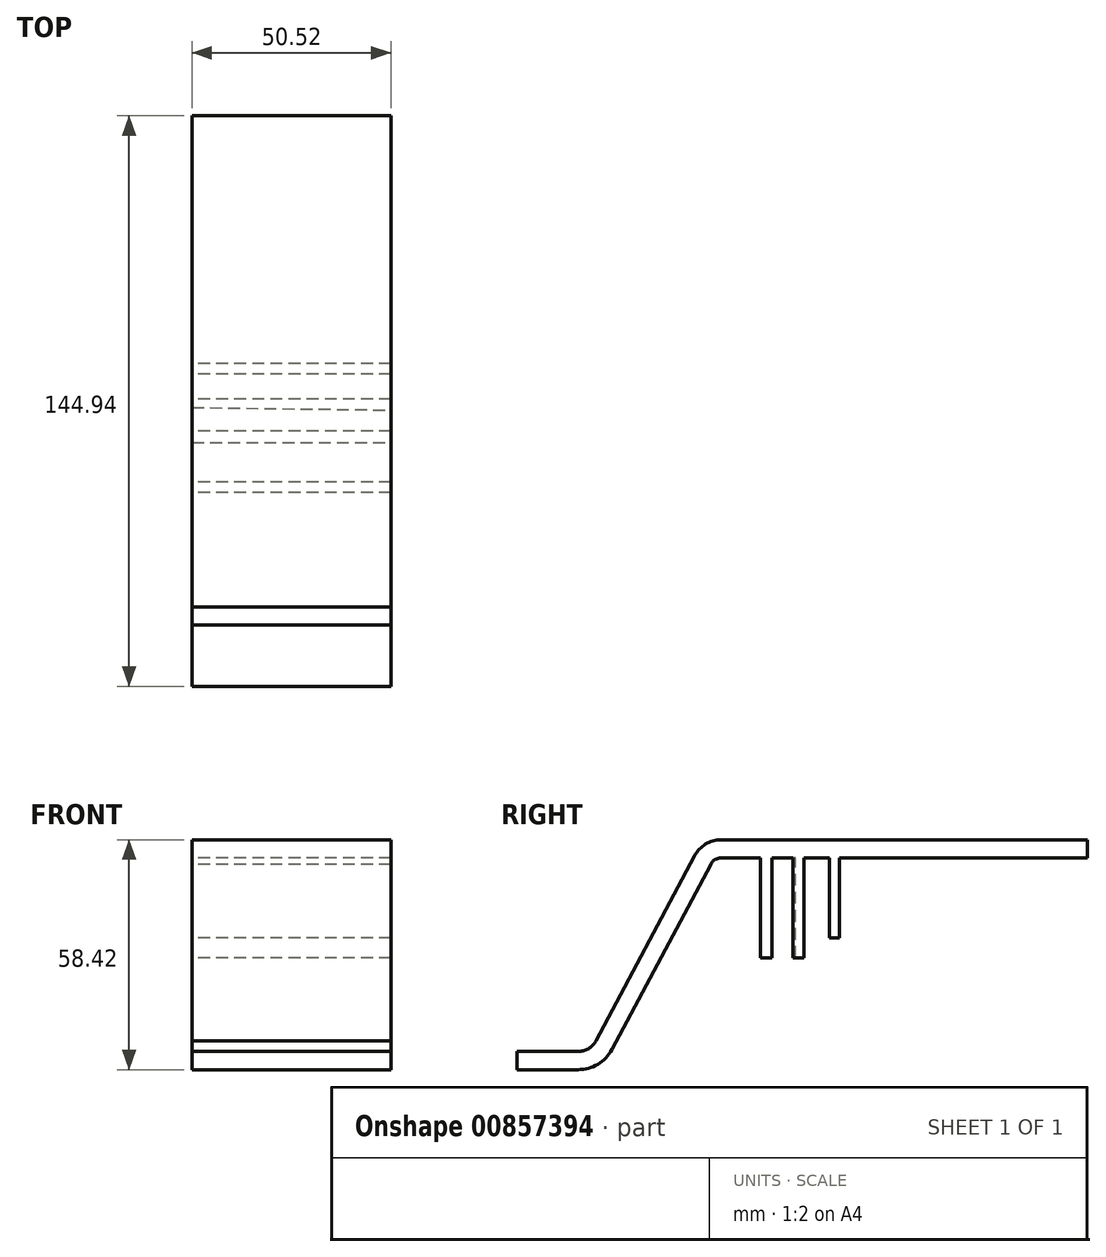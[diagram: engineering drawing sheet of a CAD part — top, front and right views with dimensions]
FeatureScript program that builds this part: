
annotation { "Feature Type Name" : "Feature", "Feature Type Description" : "" }
export const myFeature = defineFeature(function(context is Context, id is Id, definition is map)
    precondition{}
    {
        {
            var Q0;
            Q0=qCreatedBy(makeId("Right.planeOp"),FACE);
            var sketch = newSketch(context, id + "F0", { "sketchPlane" : qUnion([Q0])});
            skLineSegment(sketch, "E0", {"start": v(-55.82, -18.7) * mm, "end": v(-40.29, -18.7) * mm});
            skLineSegment(sketch, "E1", {"start": v(-34.68, -15.33) * mm, "end": v(-9.58, 31.73) * mm});
            skLineSegment(sketch, "E2", {"start": v(-3.98, 35.1) * mm, "end": v(89.12, 35.1) * mm});
            skPoint(sketch, "E3.visualSharp", {"position": v(-7.79, 35.1) * mm});
            skArc(sketch, "E3.filletArc", {"start": v(-3.98, 35.1) * mm, "mid": v(-7.24, 34.2) * mm, "end": v(-9.58, 31.73) * mm});
            skPoint(sketch, "E4.visualSharp", {"position": v(-36.48, -18.7) * mm});
            skArc(sketch, "E4.filletArc", {"start": v(-40.29, -18.7) * mm, "mid": v(-37.02, -17.8) * mm, "end": v(-34.68, -15.33) * mm});
            skSolve(sketch);
        }
        {
            var Q0;
            Q0=qCreatedBy(makeId("Front.planeOp"),FACE);
            cPlane(context, id + "F1", {"entities" : qUnion([Q0]), "cplaneType" : CPlaneType.OFFSET, "offset" : 55.88 * mm, "width" : 152.4 * mm, "height" : 152.4 * mm});
        }
        {
            var Q0;
            Q0=qCreatedBy(id+"F1.planeOp",FACE);
            var sketch = newSketch(context, id + "F2", { "sketchPlane" : qUnion([Q0])});
            skLineSegment(sketch, "E5.bottom", {"start": v(10.93, -17.45) * mm, "end": v(-39.59, -17.45) * mm});
            skLineSegment(sketch, "E5.top", {"start": v(10.93, -22.08) * mm, "end": v(-39.59, -22.08) * mm});
            skLineSegment(sketch, "E5.left", {"start": v(10.93, -17.45) * mm, "end": v(10.93, -22.08) * mm});
            skLineSegment(sketch, "E5.right", {"start": v(-39.59, -17.45) * mm, "end": v(-39.59, -22.08) * mm});
            skPoint(sketch, "E5.middle", {"position": v(-14.33, -19.77) * mm});
            skSolve(sketch);
        }
        {
            var Q0;
            Q0=makeQuery(id+"F2.imprint","IMPRINT",FACE,{"disambiguationData":[TD([[makeQuery(id+"F2.imprint","IMPRINT",EDGE,{"derivedFrom":sQuery(id+"F2.wireOp",EDGE,"E5.bottom")}),1.0]])]});
            var Q1;
            Q1=sQuery(id+"F0.wireOp",EDGE,"E0");
            var Q2;
            Q2=sQuery(id+"F0.wireOp",EDGE,"E4.filletArc");
            var Q3;
            Q3=sQuery(id+"F0.wireOp",EDGE,"E1");
            var Q4;
            Q4=sQuery(id+"F0.wireOp",EDGE,"E3.filletArc");
            var Q5;
            Q5=sQuery(id+"F0.wireOp",EDGE,"E2");
            sweep(context, id + "F3", {"profiles" : qUnion([Q0]), "path" : qUnion([Q1, Q2, Q3, Q4, Q5])});
        }
        {
            var Q0;
            Q0=makeQuery(id+"F3.opSweep","SWEPT_FACE",FACE,{"disambiguationData":[OSD([sQuery(id+"F0.wireOp",EDGE,"E2"),sQuery(id+"F2.wireOp",EDGE,"E5.top")])]});
            var sketch = newSketch(context, id + "F4", { "sketchPlane" : qUnion([Q0])});
            skLineSegment(sketch, "E6", {"start": v(10.93, -5.99) * mm, "end": v(10.93, -8.92) * mm});
            skLineSegment(sketch, "E7", {"start": v(10.93, -8.92) * mm, "end": v(-39.59, -8.92) * mm});
            skLineSegment(sketch, "E8", {"start": v(-39.59, -8.92) * mm, "end": v(-39.59, -5.99) * mm});
            skLineSegment(sketch, "E9", {"start": v(-39.59, -5.99) * mm, "end": v(10.93, -5.99) * mm});
            skLineSegment(sketch, "E10", {"start": v(10.93, -14.29) * mm, "end": v(10.93, -17.03) * mm});
            skLineSegment(sketch, "E11", {"start": v(10.93, -17.03) * mm, "end": v(-39.59, -17.03) * mm});
            skLineSegment(sketch, "E12", {"start": v(-39.59, -17.03) * mm, "end": v(-39.59, -14.93) * mm});
            skLineSegment(sketch, "E13", {"start": v(-39.59, -14.93) * mm, "end": v(10.93, -14.29) * mm});
            skLineSegment(sketch, "E14", {"start": v(10.93, -23.48) * mm, "end": v(10.93, -26.07) * mm});
            skLineSegment(sketch, "E15", {"start": v(10.93, -26.07) * mm, "end": v(-39.59, -26.07) * mm});
            skLineSegment(sketch, "E16", {"start": v(10.93, -23.48) * mm, "end": v(-39.59, -23.48) * mm});
            skLineSegment(sketch, "E17", {"start": v(-39.59, -23.48) * mm, "end": v(-39.59, -26.07) * mm});
            skSolve(sketch);
        }
        {
            var Q0;
            Q0=makeQuery(id+"F4.imprint","IMPRINT",FACE,{"disambiguationData":[TD([[makeQuery(id+"F4.imprint","IMPRINT",EDGE,{"derivedFrom":sQuery(id+"F4.wireOp",EDGE,"E6")}),-1.0]])]});
            extrude(context, id + "F5", {"entities" : qUnion([Q0]), "operationType" : NewBodyOperationType.ADD, "depth" : 20.07 * mm, "offsetDistance" : 25.4 * mm});
        }
        {
            var Q0;
            Q0=makeQuery(id+"F4.imprint","IMPRINT",FACE,{"disambiguationData":[TD([[makeQuery(id+"F4.imprint","IMPRINT",EDGE,{"derivedFrom":sQuery(id+"F4.wireOp",EDGE,"E6")}),-1.0]])]});
            var Q1;
            Q1=makeQuery(id+"F4.imprint","IMPRINT",FACE,{"disambiguationData":[TD([[makeQuery(id+"F4.imprint","IMPRINT",EDGE,{"derivedFrom":sQuery(id+"F4.wireOp",EDGE,"E10")}),-1.0]])]});
            extrude(context, id + "F6", {"entities" : qUnion([Q0, Q1]), "operationType" : NewBodyOperationType.ADD, "depth" : 25.4 * mm, "offsetDistance" : 25.4 * mm});
        }
        {
            var Q0;
            Q0=makeQuery(id+"F4.imprint","IMPRINT",FACE,{"disambiguationData":[TD([[makeQuery(id+"F4.imprint","IMPRINT",EDGE,{"derivedFrom":sQuery(id+"F4.wireOp",EDGE,"E14")}),-1.0]])]});
            extrude(context, id + "F7", {"entities" : qUnion([Q0]), "operationType" : NewBodyOperationType.ADD, "depth" : 20.32 * mm, "offsetDistance" : 25.4 * mm});
        }
    });
